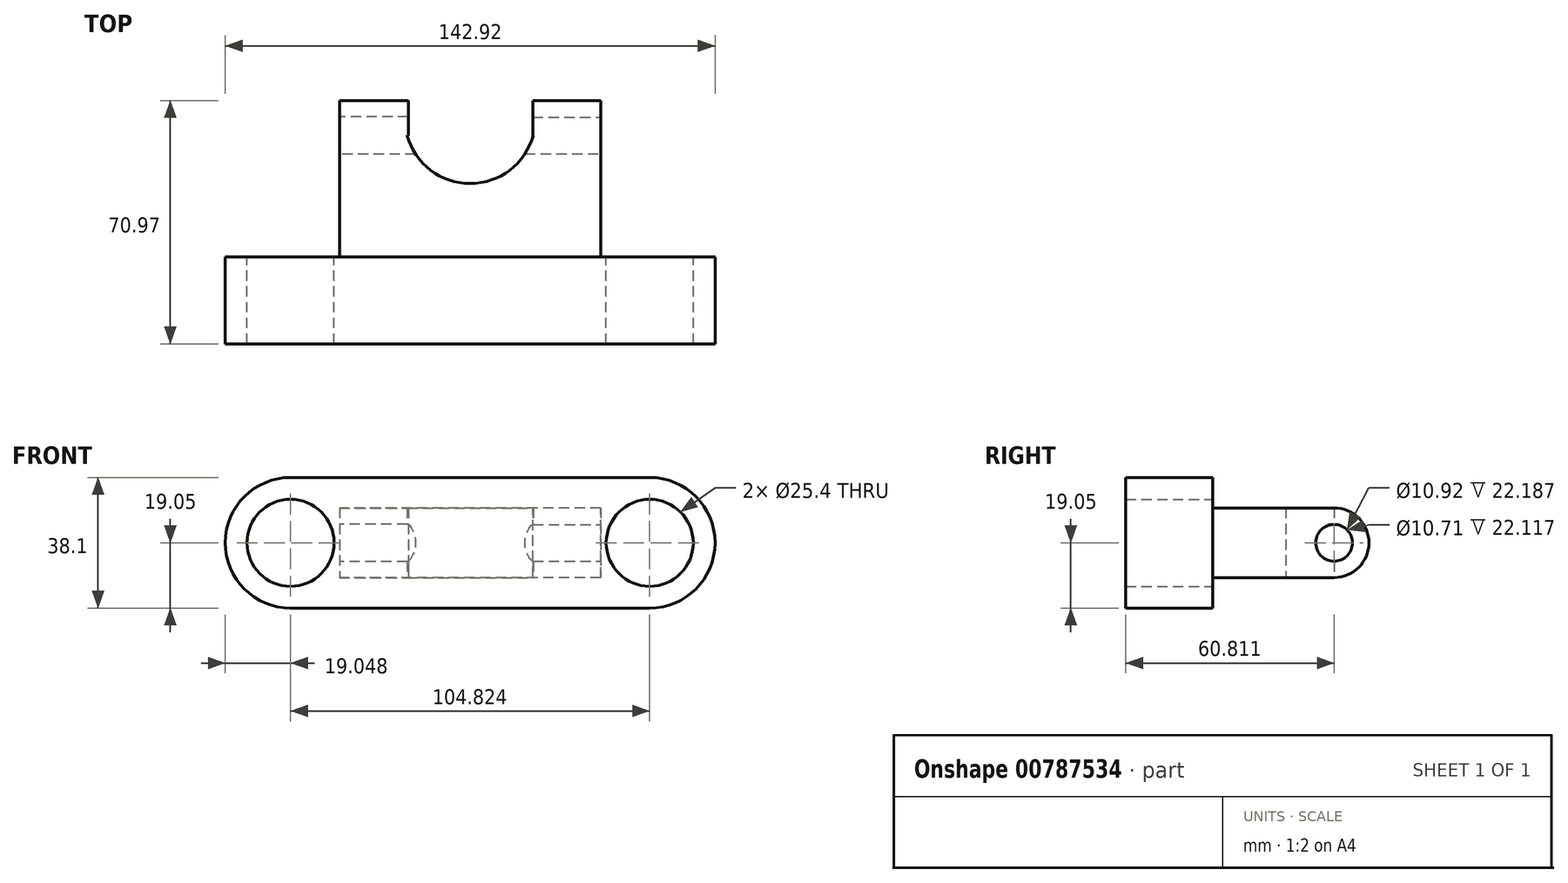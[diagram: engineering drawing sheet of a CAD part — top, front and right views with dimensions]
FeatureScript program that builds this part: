
annotation { "Feature Type Name" : "Feature", "Feature Type Description" : "" }
export const myFeature = defineFeature(function(context is Context, id is Id, definition is map)
    precondition{}
    {
        {
            var Q0;
            Q0=qCreatedBy(makeId("Front.planeOp"),FACE);
            var sketch = newSketch(context, id + "F0", { "sketchPlane" : qUnion([Q0])});
            skCircle(sketch, "E0", {"center": v(-52.41, 0) * mm, "radius": 12.7 * mm});
            skCircle(sketch, "E1", {"center": v(-52.41, 0) * mm, "radius": 19.05 * mm});
            skCircle(sketch, "E2", {"center": v(52.41, 0) * mm, "radius": 12.7 * mm});
            skCircle(sketch, "E3", {"center": v(52.41, 0) * mm, "radius": 19.05 * mm});
            skLineSegment(sketch, "E4", {"start": v(-52.41, 19.05) * mm, "end": v(52.41, 19.05) * mm});
            skLineSegment(sketch, "E5", {"start": v(52.41, -19.05) * mm, "end": v(-52.41, -19.05) * mm});
            skSolve(sketch);
        }
        {
            var Q0;
            {var subQ0=sQuery(id+"F0.wireOp",EDGE,"E4");Q0=makeQuery(id+"F0.imprint","IMPRINT",FACE,{"disambiguationData":[TD([[makeQuery(id+"F0.imprint","IMPRINT",EDGE,{"derivedFrom":subQ0}),-1.0]])]});}
            var Q1;
            Q1=makeQuery(id+"F0.imprint","IMPRINT",FACE,{"disambiguationData":[TD([[makeQuery(id+"F0.imprint","IMPRINT",EDGE,{"derivedFrom":sQuery(id+"F0.wireOp",EDGE,"E0")}),-1.0]])]});
            var Q2;
            Q2=makeQuery(id+"F0.imprint","IMPRINT",FACE,{"disambiguationData":[TD([[makeQuery(id+"F0.imprint","IMPRINT",EDGE,{"derivedFrom":sQuery(id+"F0.wireOp",EDGE,"E2")}),-1.0]])]});
            extrude(context, id + "F1", {"entities" : qUnion([Q0, Q1, Q2]), "depth" : 25.4 * mm, "offsetDistance" : 25.4 * mm});
        }
        {
            var Q0;
            Q0=qCreatedBy(makeId("Top.planeOp"),FACE);
            var sketch = newSketch(context, id + "F2", { "sketchPlane" : qUnion([Q0])});
            skLineSegment(sketch, "E6", {"start": v(0, 0) * mm, "end": v(-38.1, 0) * mm});
            skLineSegment(sketch, "E7", {"start": v(-38.1, 0) * mm, "end": v(-38.1, 35.41) * mm});
            skLineSegment(sketch, "E8", {"start": v(-38.1, 35.41) * mm, "end": v(-18.38, 35.41) * mm});
            skLineSegment(sketch, "E9", {"start": v(0, 0) * mm, "end": v(38.1, 0) * mm});
            skLineSegment(sketch, "E10", {"start": v(38.1, 0) * mm, "end": v(38.1, 35.41) * mm});
            skLineSegment(sketch, "E11", {"start": v(38.1, 35.41) * mm, "end": v(18.38, 35.41) * mm});
            skArc(sketch, "E12", {"start": v(-18.38, 35.41) * mm, "mid": v(0, 21.36) * mm, "end": v(18.38, 35.41) * mm});
            skSolve(sketch);
        }
        {
            var Q0;
            Q0=makeQuery(id+"F2.imprint","IMPRINT",FACE,{"disambiguationData":[TD([[makeQuery(id+"F2.imprint","IMPRINT",EDGE,{"derivedFrom":sQuery(id+"F2.wireOp",EDGE,"E6")}),-1.0]])]});
            extrude(context, id + "F3", {"entities" : qUnion([Q0]), "operationType" : NewBodyOperationType.ADD, "depth" : 10.16 * mm, "offsetDistance" : 25.4 * mm});
        }
        {
            var Q0;
            Q0=makeQuery(id+"F3.opExtrude","CAP_FACE",FACE,{"disambiguationData":[OSD([sQuery(id+"F2.wireOp",EDGE,"E6"),sQuery(id+"F2.wireOp",EDGE,"E7"),sQuery(id+"F2.wireOp",EDGE,"E8"),sQuery(id+"F2.wireOp",EDGE,"E9"),sQuery(id+"F2.wireOp",EDGE,"E10"),sQuery(id+"F2.wireOp",EDGE,"E11"),sQuery(id+"F2.wireOp",EDGE,"E12")])],"isStart":true});
            extrude(context, id + "F4", {"entities" : qUnion([Q0]), "operationType" : NewBodyOperationType.ADD, "depth" : 10.16 * mm, "offsetDistance" : 25.4 * mm});
        }
        {
            var Q0;
            {var subQ0=sQuery(id+"F2.wireOp",EDGE,"E7");Q0=makeQuery(id+"F4.boolean.opBoolean","MERGE",FACE,{"derivedFrom":[makeQuery(id+"F3.opExtrude","SWEPT_FACE",FACE,{"disambiguationData":[OSD([subQ0])]}),makeQuery(id+"F4.opExtrude","SWEPT_FACE",FACE,{"disambiguationData":[OSD([subQ0])]})]});}
            var sketch = newSketch(context, id + "F5", { "sketchPlane" : qUnion([Q0])});
            skArc(sketch, "E13", {"start": v(-35.41, 10.16) * mm, "mid": v(-45.57, 0) * mm, "end": v(-35.41, -10.16) * mm});
            skSolve(sketch);
        }
        {
            var Q0;
            Q0=makeQuery(id+"F5.imprint","IMPRINT",FACE,{"disambiguationData":[TD([[makeQuery(id+"F5.imprint","IMPRINT",EDGE,{"derivedFrom":sQuery(id+"F5.wireOp",EDGE,"E13")}),1.0]])]});
            extrude(context, id + "F6", {"entities" : qUnion([Q0]), "operationType" : NewBodyOperationType.ADD, "oppositeDirection" : true, "depth" : 20.07 * mm, "offsetDistance" : 25.4 * mm});
        }
        {
            var Q0;
            {var subQ0=sQuery(id+"F2.wireOp",EDGE,"E10");Q0=makeQuery(id+"F4.boolean.opBoolean","MERGE",FACE,{"derivedFrom":[makeQuery(id+"F3.opExtrude","SWEPT_FACE",FACE,{"disambiguationData":[OSD([subQ0])]}),makeQuery(id+"F4.opExtrude","SWEPT_FACE",FACE,{"disambiguationData":[OSD([subQ0])]})]});}
            var sketch = newSketch(context, id + "F7", { "sketchPlane" : qUnion([Q0])});
            skArc(sketch, "E14", {"start": v(35.41, -10.16) * mm, "mid": v(45.57, 0) * mm, "end": v(35.41, 10.16) * mm});
            skSolve(sketch);
        }
        {
            var Q0;
            Q0=makeQuery(id+"F7.imprint","IMPRINT",FACE,{"disambiguationData":[TD([[makeQuery(id+"F7.imprint","IMPRINT",EDGE,{"derivedFrom":sQuery(id+"F7.wireOp",EDGE,"E14")}),1.0]])]});
            extrude(context, id + "F8", {"entities" : qUnion([Q0]), "operationType" : NewBodyOperationType.ADD, "oppositeDirection" : true, "depth" : 19.8 * mm, "offsetDistance" : 25.4 * mm});
        }
        {
            var Q0;
            {var subQ0=sQuery(id+"F2.wireOp",EDGE,"E7");Q0=makeQuery(id+"F6.boolean.opBoolean","MERGE",FACE,{"derivedFrom":[makeQuery(id+"F4.boolean.opBoolean","MERGE",FACE,{"derivedFrom":[makeQuery(id+"F3.opExtrude","SWEPT_FACE",FACE,{"disambiguationData":[OSD([subQ0])]}),makeQuery(id+"F4.opExtrude","SWEPT_FACE",FACE,{"disambiguationData":[OSD([subQ0])]})]}),makeQuery(id+"F6.opExtrude","CAP_FACE",FACE,{"disambiguationData":[OSD([subQ0,sQuery(id+"F2.wireOp",EDGE,"E8"),sQuery(id+"F5.wireOp",EDGE,"E13")])],"isStart":true})]});}
            var sketch = newSketch(context, id + "F9", { "sketchPlane" : qUnion([Q0])});
            skCircle(sketch, "E15", {"center": v(-35.41, 0) * mm, "radius": 5.46 * mm});
            skSolve(sketch);
        }
        {
            var Q0;
            {var subQ0=sQuery(id+"F2.wireOp",EDGE,"E10");Q0=makeQuery(id+"F8.boolean.opBoolean","MERGE",FACE,{"derivedFrom":[makeQuery(id+"F4.boolean.opBoolean","MERGE",FACE,{"derivedFrom":[makeQuery(id+"F3.opExtrude","SWEPT_FACE",FACE,{"disambiguationData":[OSD([subQ0])]}),makeQuery(id+"F4.opExtrude","SWEPT_FACE",FACE,{"disambiguationData":[OSD([subQ0])]})]}),makeQuery(id+"F8.opExtrude","CAP_FACE",FACE,{"disambiguationData":[OSD([subQ0,sQuery(id+"F2.wireOp",EDGE,"E11"),sQuery(id+"F7.wireOp",EDGE,"E14")])],"isStart":true})]});}
            var sketch = newSketch(context, id + "F10", { "sketchPlane" : qUnion([Q0])});
            skCircle(sketch, "E16", {"center": v(35.41, 0) * mm, "radius": 5.35 * mm});
            skSolve(sketch);
        }
        {
            var Q0;
            Q0=makeQuery(id+"F9.imprint","IMPRINT",FACE,{"disambiguationData":[TD([[makeQuery(id+"F9.imprint","IMPRINT",EDGE,{"derivedFrom":sQuery(id+"F9.wireOp",EDGE,"E15")}),1.0]])]});
            extrude(context, id + "F11", {"entities" : qUnion([Q0]), "operationType" : NewBodyOperationType.REMOVE, "oppositeDirection" : true, "depth" : 25.4 * mm, "offsetDistance" : 25.4 * mm});
        }
        {
            var Q0;
            Q0=makeQuery(id+"F10.imprint","IMPRINT",FACE,{"disambiguationData":[TD([[makeQuery(id+"F10.imprint","IMPRINT",EDGE,{"derivedFrom":sQuery(id+"F10.wireOp",EDGE,"E16")}),1.0]])]});
            extrude(context, id + "F12", {"entities" : qUnion([Q0]), "operationType" : NewBodyOperationType.REMOVE, "oppositeDirection" : true, "depth" : 25.4 * mm, "offsetDistance" : 25.4 * mm});
        }
    });
